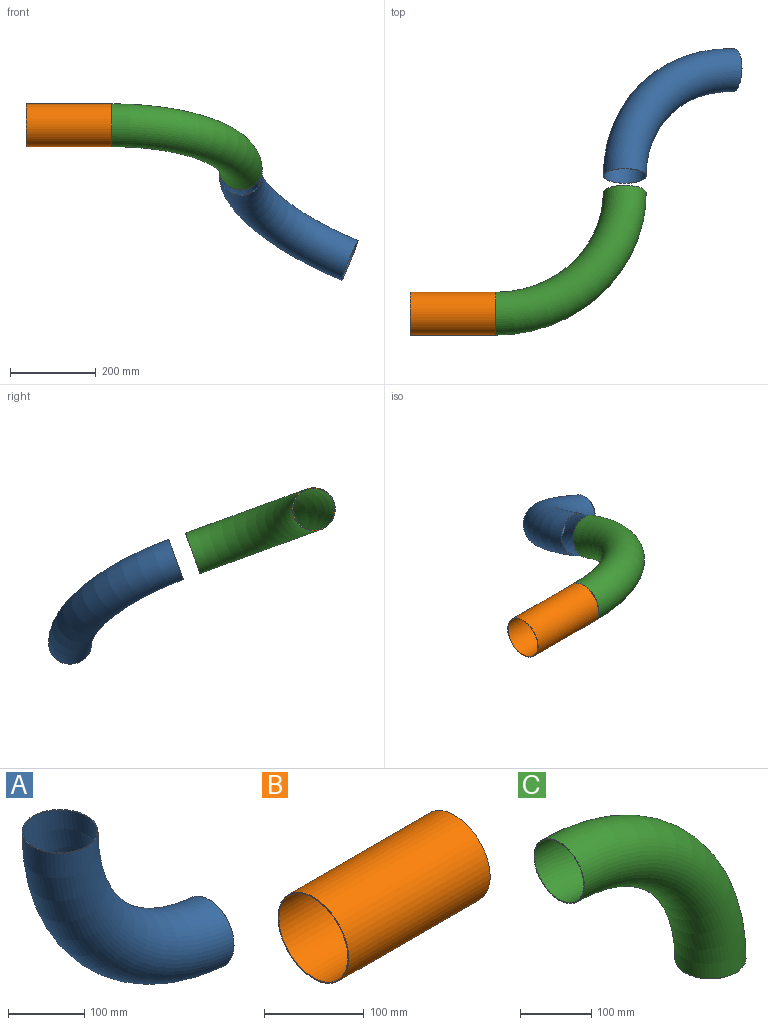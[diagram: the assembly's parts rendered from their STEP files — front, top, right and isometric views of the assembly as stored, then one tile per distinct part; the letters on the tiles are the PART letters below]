
ASSEMBLY  parts=3 mates=2
PART A: 4 faces, bbox 356.8x100x377.4 mm
  f0: torus R=300mm, axis (0,-1,0), area 136242.3mm2, adj f1,f2
  f1: plane 100x100mm, normal (0,0,1), area 387.8mm2, adj f0,f3
  f2: plane 100x99.61mm, normal (1,0,-0.09), area 387.8mm2, adj f0,f3
  f3: torus R=300mm, axis (0,-1,0), area 139735.7mm2, adj f1,f2
PART B: 4 faces, bbox 200x100x100 mm
  f0: cylinder r=48.75mm len=200mm, axis (1,0,0), area 61261.1mm2, adj f1,f2
  f1: plane 100x100mm, normal (-1,0,0), area 387.8mm2, adj f0,f3
  f2: plane 100x100mm, normal (1,0,0), area 387.8mm2, adj f0,f3
  f3: cylinder r=50mm len=200mm, axis (1,0,0), area 62831.9mm2, adj f1,f2
PART C: 4 faces, bbox 378.8x100x378.8 mm
  f0: torus R=300mm, axis (0,1,0), area 144343mm2, adj f1,f2
  f1: plane 100x100mm, normal (-1,0,0), area 387.8mm2, adj f0,f3
  f2: plane 100x100mm, normal (0,0,-1), area 387.8mm2, adj f0,f3
  f3: torus R=300mm, axis (0,1,0), area 148044.1mm2, adj f1,f2
PLACE A rot(axis=(0.95,0.18,-0.26),72.9deg) t=(35.76,-155,314.02)mm
PLACE B at identity fixed
PLACE C rot(axis=(1,0,0),70deg) t=(0,56.38,39.48)mm
MATE cylindrical C.f2 <-> A.f1  axis (0,0.94,-0.34) through (500,281.91,-42.61)mm
MATE revolute B.f0 <-> C.f1  axis (1,0,0) through (200,0,60)mm
